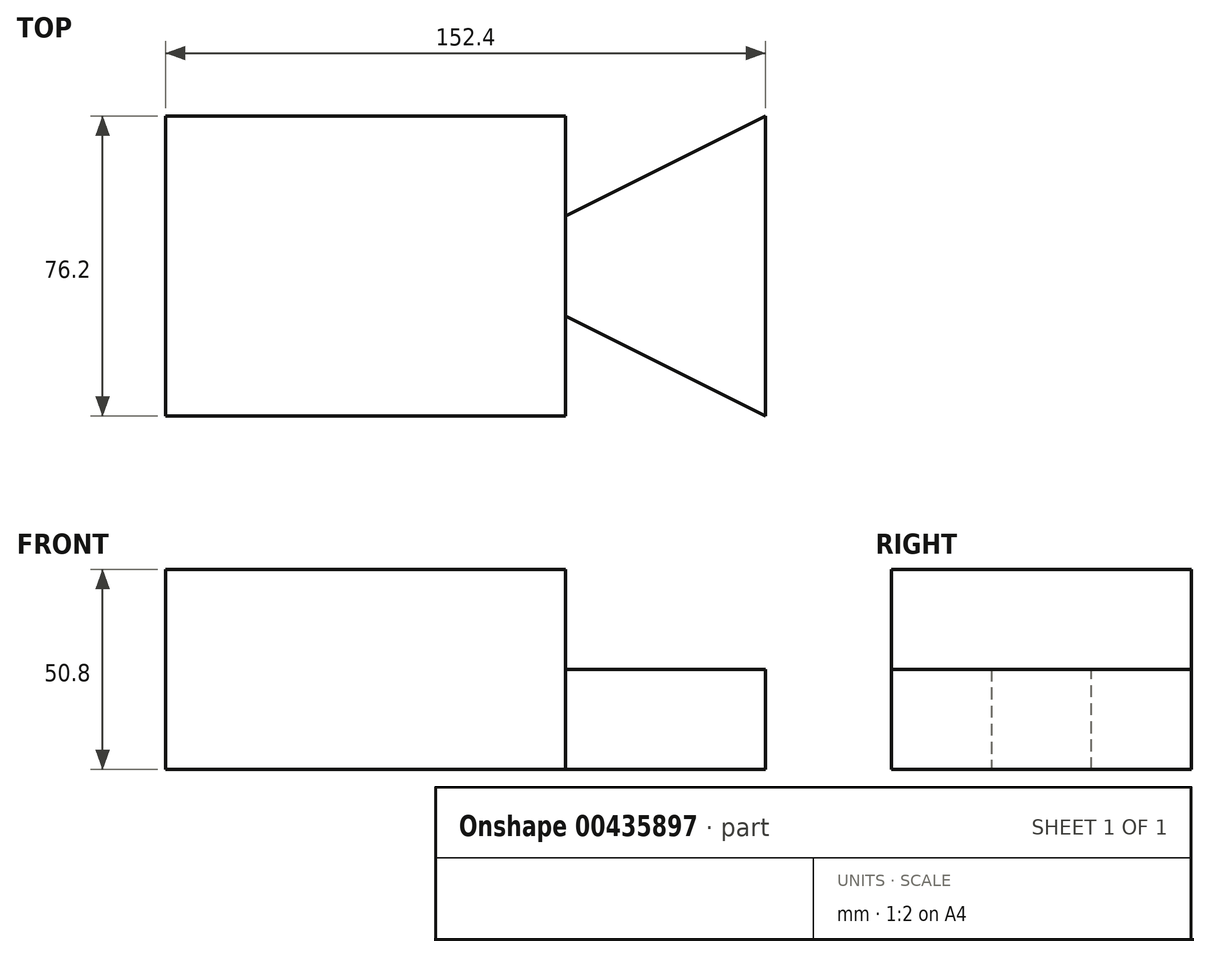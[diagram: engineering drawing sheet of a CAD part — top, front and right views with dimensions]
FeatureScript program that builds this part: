
annotation { "Feature Type Name" : "Feature", "Feature Type Description" : "" }
export const myFeature = defineFeature(function(context is Context, id is Id, definition is map)
    precondition{}
    {
        {
            var Q0;
            Q0=qCreatedBy(makeId("Front.planeOp"),FACE);
            var sketch = newSketch(context, id + "F0", { "sketchPlane" : qUnion([Q0])});
            skLineSegment(sketch, "E0", {"start": v(0, 0) * mm, "end": v(152.4, 0) * mm});
            skLineSegment(sketch, "E1", {"start": v(0, 0) * mm, "end": v(0, 50.8) * mm});
            skLineSegment(sketch, "E2", {"start": v(0, 50.8) * mm, "end": v(152.4, 50.8) * mm});
            skLineSegment(sketch, "E3", {"start": v(152.4, 50.8) * mm, "end": v(152.4, 0) * mm});
            skSolve(sketch);
        }
        {
            var Q0;
            Q0=makeQuery(id+"F0.imprint","IMPRINT",FACE,{"disambiguationData":[TD([[makeQuery(id+"F0.imprint","IMPRINT",EDGE,{"derivedFrom":sQuery(id+"F0.wireOp",EDGE,"E0")}),1.0]])]});
            var sketch = newSketch(context, id + "F1", { "sketchPlane" : qUnion([Q0])});
            skLineSegment(sketch, "E4", {"start": v(0, 0) * mm, "end": v(152.4, 0) * mm});
            skLineSegment(sketch, "E5", {"start": v(152.4, 0) * mm, "end": v(152.4, 50.8) * mm});
            skLineSegment(sketch, "E6", {"start": v(152.4, 50.8) * mm, "end": v(101.6, 50.8) * mm});
            skLineSegment(sketch, "E7", {"start": v(101.6, 50.8) * mm, "end": v(101.6, 25.4) * mm});
            skLineSegment(sketch, "E8", {"start": v(101.6, 25.4) * mm, "end": v(152.4, 25.4) * mm});
            skSolve(sketch);
        }
        {
            var Q0;
            Q0=makeQuery(id+"F0.imprint","IMPRINT",FACE,{"disambiguationData":[TD([[makeQuery(id+"F0.imprint","IMPRINT",EDGE,{"derivedFrom":sQuery(id+"F0.wireOp",EDGE,"E0")}),1.0]])]});
            extrude(context, id + "F2", {"entities" : qUnion([Q0]), "oppositeDirection" : true, "depth" : 76.2 * mm});
        }
        {
            var Q0;
            {var subQ0=sQuery(id+"F1.wireOp",EDGE,"E6");Q0=makeQuery(id+"F1.imprint","IMPRINT",FACE,{"disambiguationData":[TD([[makeQuery(id+"F1.imprint","IMPRINT",EDGE,{"derivedFrom":subQ0}),-1.0]])]});}
            extrude(context, id + "F3", {"entities" : qUnion([Q0]), "operationType" : NewBodyOperationType.REMOVE, "oppositeDirection" : true, "depth" : 76.2 * mm});
        }
        {
            var Q0;
            Q0=qCreatedBy(makeId("Top.planeOp"),FACE);
            var sketch = newSketch(context, id + "F4", { "sketchPlane" : qUnion([Q0])});
            skLineSegment(sketch, "E9", {"start": v(0, 0) * mm, "end": v(101.6, 0) * mm});
            skLineSegment(sketch, "E10", {"start": v(101.6, 0) * mm, "end": v(101.6, 25.4) * mm});
            skLineSegment(sketch, "E11", {"start": v(101.6, 0) * mm, "end": v(152.4, 0) * mm});
            skLineSegment(sketch, "E12", {"start": v(101.6, 25.4) * mm, "end": v(152.4, 0) * mm});
            skLineSegment(sketch, "E13", {"start": v(0, 0) * mm, "end": v(0, 76.2) * mm});
            skLineSegment(sketch, "E14", {"start": v(0, 76.2) * mm, "end": v(101.6, 76.2) * mm});
            skLineSegment(sketch, "E15", {"start": v(101.6, 76.2) * mm, "end": v(152.4, 76.2) * mm});
            skLineSegment(sketch, "E16", {"start": v(101.6, 76.2) * mm, "end": v(101.6, 50.8) * mm});
            skLineSegment(sketch, "E17", {"start": v(101.6, 50.8) * mm, "end": v(152.4, 76.2) * mm});
            skSolve(sketch);
        }
        {
            var Q0;
            Q0=makeQuery(id+"F4.imprint","IMPRINT",FACE,{"disambiguationData":[TD([[makeQuery(id+"F4.imprint","IMPRINT",EDGE,{"derivedFrom":sQuery(id+"F4.wireOp",EDGE,"E10")}),-1.0]])]});
            extrude(context, id + "F5", {"entities" : qUnion([Q0]), "operationType" : NewBodyOperationType.REMOVE, "depth" : 25.4 * mm});
        }
        {
            var Q0;
            Q0=makeQuery(id+"F3.boolean.opBoolean","COPY",FACE,{"derivedFrom":makeQuery(id+"F3.opExtrude","SWEPT_FACE",FACE,{"disambiguationData":[OSD([sQuery(id+"F1.wireOp",EDGE,"E8")])]})});
            var sketch = newSketch(context, id + "F6", { "sketchPlane" : qUnion([Q0])});
            skLineSegment(sketch, "E18", {"start": v(101.6, 76.2) * mm, "end": v(101.6, 50.8) * mm});
            skLineSegment(sketch, "E19", {"start": v(101.6, 76.2) * mm, "end": v(152.4, 76.2) * mm});
            skLineSegment(sketch, "E20", {"start": v(152.4, 76.2) * mm, "end": v(101.6, 50.8) * mm});
            skSolve(sketch);
        }
        {
            var Q0;
            Q0=makeQuery(id+"F6.imprint","IMPRINT",FACE,{"disambiguationData":[TD([[makeQuery(id+"F6.imprint","IMPRINT",EDGE,{"derivedFrom":sQuery(id+"F6.wireOp",EDGE,"E18")}),1.0]])]});
            extrude(context, id + "F7", {"entities" : qUnion([Q0]), "operationType" : NewBodyOperationType.REMOVE, "oppositeDirection" : true, "depth" : 25.4 * mm});
        }
    });
